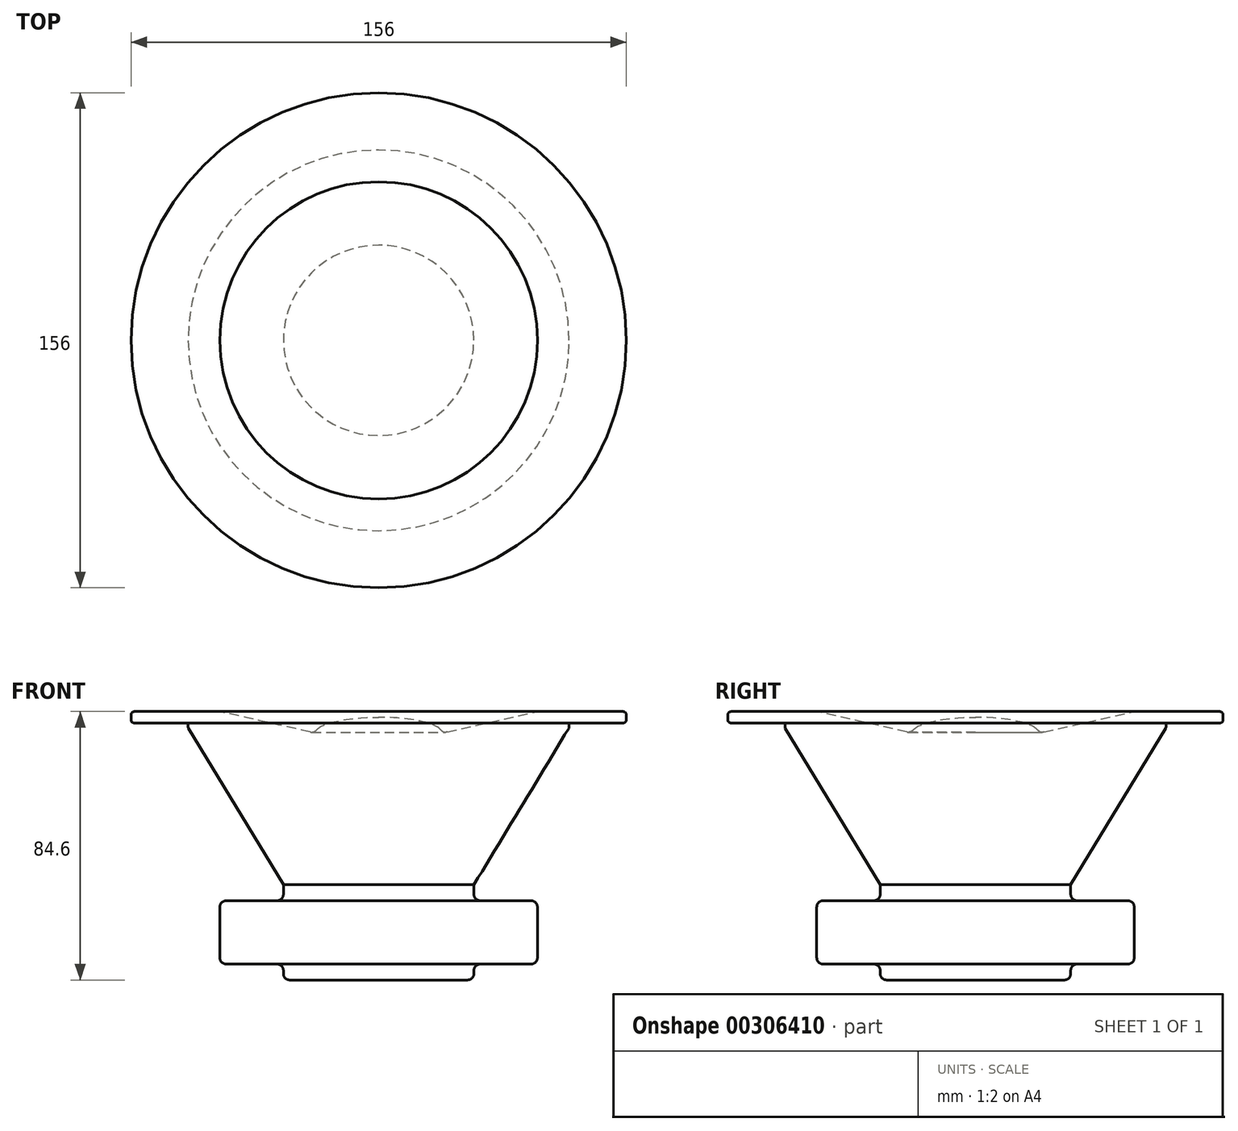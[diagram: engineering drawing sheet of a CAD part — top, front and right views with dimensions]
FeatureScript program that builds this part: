
annotation { "Feature Type Name" : "Feature", "Feature Type Description" : "" }
export const myFeature = defineFeature(function(context is Context, id is Id, definition is map)
    precondition{}
    {
        {
            var Q0;
            Q0=qCreatedBy(makeId("Front.planeOp"),FACE);
            var sketch = newSketch(context, id + "F0", { "sketchPlane" : qUnion([Q0])});
            skLineSegment(sketch, "E0.bottom", {"start": v(0, 1.8) * mm, "end": v(-77, 1.8) * mm});
            skLineSegment(sketch, "E0.top", {"start": v(-60.5, -1.8) * mm, "end": v(-77, -1.8) * mm});
            skLineSegment(sketch, "E0.right", {"start": v(-78, 0.8) * mm, "end": v(-78, -0.8) * mm});
            skPoint(sketch, "E0.middle", {"position": v(0, 0) * mm});
            skLineSegment(sketch, "E1", {"start": v(0, -1.8) * mm, "end": v(0, -82.8) * mm});
            skPoint(sketch, "E1.endSnap0", {"position": v(0, -1.8) * mm});
            skLineSegment(sketch, "E2.left", {"start": v(0, -82.8) * mm, "end": v(0, -52.8) * mm});
            skLineSegment(sketch, "E3.bottom", {"start": v(0, -82.8) * mm, "end": v(-28, -82.8) * mm});
            skLineSegment(sketch, "E3.top", {"start": v(0, -52.8) * mm, "end": v(-30, -52.8) * mm});
            skLineSegment(sketch, "E3.right", {"start": v(-50, -75.8) * mm, "end": v(-50, -59.8) * mm});
            skLineSegment(sketch, "E4.left", {"start": v(0, -1.8) * mm, "end": v(0, -3.3) * mm});
            skLineSegment(sketch, "E5.bottom", {"start": v(0, -3.3) * mm, "end": v(-60, -3.3) * mm});
            skLineSegment(sketch, "E5.top", {"start": v(0, -1.8) * mm, "end": v(-60, -1.8) * mm});
            skLineSegment(sketch, "E5.left", {"start": v(0, -3.3) * mm, "end": v(0, -1.8) * mm});
            skLineSegment(sketch, "E5.right", {"start": v(-60, -3.16) * mm, "end": v(-60, -2.3) * mm});
            skLineSegment(sketch, "E6.left", {"start": v(50, -57.8) * mm, "end": v(50, -58.16) * mm});
            skLineSegment(sketch, "E7.top", {"start": v(-48, -77.8) * mm, "end": v(-32, -77.8) * mm});
            skLineSegment(sketch, "E7.right", {"start": v(-30, -80.8) * mm, "end": v(-30, -79.8) * mm});
            skLineSegment(sketch, "E8.top", {"start": v(-48, -57.8) * mm, "end": v(-32, -57.8) * mm});
            skLineSegment(sketch, "E8.right", {"start": v(-30, -52.8) * mm, "end": v(-30, -55.8) * mm});
            skLineSegment(sketch, "E9", {"start": v(-59.93, -3.42) * mm, "end": v(-30, -52.8) * mm});
            skPoint(sketch, "E10.orphan", {"position": v(-50, -52.8) * mm});
            skLineSegment(sketch, "E11.bottom", {"start": v(-50, 1.8) * mm, "end": v(-70, 1.8) * mm});
            skLineSegment(sketch, "E11.top", {"start": v(0, 11.8) * mm, "end": v(-60, 11.8) * mm});
            skLineSegment(sketch, "E11.left", {"start": v(0, 1.8) * mm, "end": v(0, 11.8) * mm});
            skLineSegment(sketch, "E11.right", {"start": v(-70, 1.8) * mm, "end": v(-70, 1.8) * mm});
            skPoint(sketch, "E12.visualSharp", {"position": v(-70, 11.8) * mm});
            skArc(sketch, "E12.filletArc", {"start": v(-60, 11.8) * mm, "mid": v(-67.07, 8.87) * mm, "end": v(-70, 1.8) * mm});
            skPoint(sketch, "E13.visualSharp", {"position": v(-50, -57.8) * mm});
            skArc(sketch, "E13.filletArc", {"start": v(-48, -57.8) * mm, "mid": v(-49.41, -58.39) * mm, "end": v(-50, -59.8) * mm});
            skPoint(sketch, "E14.visualSharp", {"position": v(-30, -77.8) * mm});
            skArc(sketch, "E14.filletArc", {"start": v(-30, -79.8) * mm, "mid": v(-30.59, -78.39) * mm, "end": v(-32, -77.8) * mm});
            skPoint(sketch, "E15.visualSharp", {"position": v(-50, -77.8) * mm});
            skArc(sketch, "E15.filletArc", {"start": v(-50, -75.8) * mm, "mid": v(-49.41, -77.21) * mm, "end": v(-48, -77.8) * mm});
            skPoint(sketch, "E16.visualSharp", {"position": v(-30, -82.8) * mm});
            skArc(sketch, "E16.filletArc", {"start": v(-30, -80.8) * mm, "mid": v(-29.41, -82.21) * mm, "end": v(-28, -82.8) * mm});
            skPoint(sketch, "E17.visualSharp", {"position": v(30, -82.8) * mm});
            skPoint(sketch, "E18.visualSharp", {"position": v(50, -78) * mm});
            skPoint(sketch, "E19.visualSharp", {"position": v(30, -78) * mm});
            skPoint(sketch, "E20.visualSharp", {"position": v(50, -57.8) * mm});
            skPoint(sketch, "E21.visualSharp", {"position": v(30, -57.8) * mm});
            skPoint(sketch, "E22.visualSharp", {"position": v(-30, -57.8) * mm});
            skArc(sketch, "E22.filletArc", {"start": v(-32, -57.8) * mm, "mid": v(-30.59, -57.21) * mm, "end": v(-30, -55.8) * mm});
            skPoint(sketch, "E23.visualSharp", {"position": v(-78, 1.8) * mm});
            skArc(sketch, "E23.filletArc", {"start": v(-77, 1.8) * mm, "mid": v(-77.7, 1.5) * mm, "end": v(-78, 0.8) * mm});
            skPoint(sketch, "E24.visualSharp", {"position": v(-78, -1.8) * mm});
            skArc(sketch, "E24.filletArc", {"start": v(-78, -0.8) * mm, "mid": v(-77.7, -1.5) * mm, "end": v(-77, -1.8) * mm});
            skPoint(sketch, "E25.newPointA", {"position": v(78, -1.8) * mm});
            skArc(sketch, "E25.filletArc", {"start": v(-60, -2.3) * mm, "mid": v(-60.15, -1.95) * mm, "end": v(-60.5, -1.8) * mm});
            skPoint(sketch, "E26.visualSharp", {"position": v(-60, -3.3) * mm});
            skArc(sketch, "E26.filletArc", {"start": v(-60, -3.16) * mm, "mid": v(-59.98, -3.3) * mm, "end": v(-59.93, -3.42) * mm});
            skPoint(sketch, "E0.left.start.orphan", {"position": v(78, 1.8) * mm});
            skLineSegment(sketch, "E27", {"start": v(-60.5, -1.8) * mm, "end": v(-60, -1.8) * mm});
            skLineSegment(sketch, "E28", {"start": v(0, 1.8) * mm, "end": v(0, -1.8) * mm});
            skPoint(sketch, "E29.visualSharp", {"position": v(-20, -5) * mm});
            skLineSegment(sketch, "E30", {"start": v(0, 0) * mm, "end": v(0, 1.8) * mm});
            skLineSegment(sketch, "E31.MirrorCS", {"start": v(0, 11.8) * mm, "end": v(60, 11.8) * mm});
            skArc(sketch, "E32.MirrorCS", {"start": v(60, 11.8) * mm, "mid": v(52.93, 8.87) * mm, "end": v(50, 1.8) * mm});
            skLineSegment(sketch, "E33.MirrorCS", {"start": v(50, 1.8) * mm, "end": v(21.56, -4.65) * mm});
            skArc(sketch, "E34.MirrorCS", {"start": v(21.56, -4.65) * mm, "mid": v(20.47, -4.6) * mm, "end": v(19.58, -3.98) * mm});
            skEllipticalArc(sketch, "E35.MirrorCS", {});
            skPoint(sketch, "E29.filletArc.end.orphan", {"position": v(-19.58, -3.98) * mm});
            skPoint(sketch, "E36.orphan", {"position": v(-21.56, -4.65) * mm});
            const initialGuessF0  = {"E35.MirrorCS": [0, -0.005, 1, 0, 0.02, 0.005, 0.20574105938796539, 1.5707963267948966]};
            skSetInitialGuess(sketch, initialGuessF0);
            skSolve(sketch);
        }
        {
            var Q0;
            Q0=makeQuery(id+"F0.imprint","IMPRINT",FACE,{"disambiguationData":[TD([[makeQuery(id+"F0.imprint","IMPRINT",EDGE,{"derivedFrom":sQuery(id+"F0.wireOp",EDGE,"E11.bottom")}),-1.0]])]});
            var Q1;
            {var subQ2=sQuery(id+"F0.wireOp",EDGE,"E1");Q1=makeQuery(id+"F0.imprint","IMPRINT",FACE,{"disambiguationData":[TD([[makeQuery(id+"F0.imprint","IMPRINT",EDGE,{"derivedFrom":subQ2}),-1.0]])]});}
            var Q2;
            Q2=makeQuery(id+"F0.imprint","IMPRINT",FACE,{"disambiguationData":[TD([[makeQuery(id+"F0.imprint","IMPRINT",EDGE,{"derivedFrom":sQuery(id+"F0.wireOp",EDGE,"E3.bottom")}),-1.0]])]});
            var Q3;
            Q3=makeQuery(id+"F0.imprint","IMPRINT",FACE,{"disambiguationData":[TD([[makeQuery(id+"F0.imprint","IMPRINT",EDGE,{"derivedFrom":sQuery(id+"F0.wireOp",EDGE,"E0.bottom")}),1.0]])]});
            var Q4;
            Q4=makeQuery(id+"F0.imprint","IMPRINT",FACE,{"disambiguationData":[TD([[makeQuery(id+"F0.imprint","IMPRINT",EDGE,{"derivedFrom":sQuery(id+"F0.wireOp",EDGE,"E5.top")}),1.0]])]});
            var Q5;
            Q5=sQuery(id+"F0.wireOp",EDGE,"E1");
            revolve(context, id + "F1", {"entities" : qUnion([Q0, Q1, Q2, Q3, Q4]), "axis" : qUnion([Q5]), "revolveType" : RevolveType.FULL});
        }
        {
            var Q0;
            {var subQ0=sQuery(id+"F0.wireOp",EDGE,"E11.left");Q0=makeQuery(id+"F0.imprint","IMPRINT",FACE,{"disambiguationData":[TD([[makeQuery(id+"F0.imprint","IMPRINT",EDGE,{"derivedFrom":subQ0}),-1.0]])]});}
            var Q1;
            Q1=sQuery(id+"F0.wireOp",EDGE,"E1");
            revolve(context, id + "F2", {"operationType" : NewBodyOperationType.REMOVE, "entities" : qUnion([Q0]), "axis" : qUnion([Q1]), "revolveType" : RevolveType.FULL, "oppositeDirection" : true});
        }
    });
